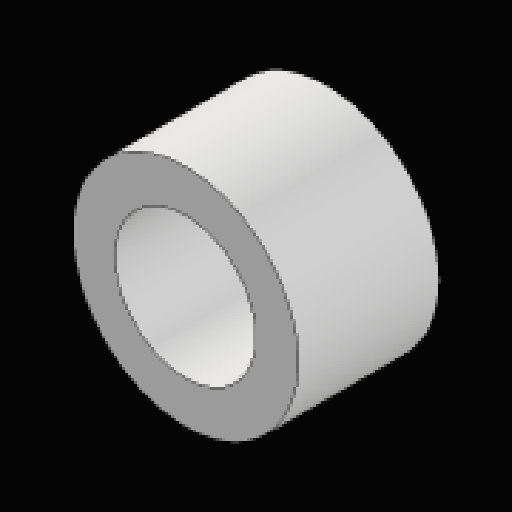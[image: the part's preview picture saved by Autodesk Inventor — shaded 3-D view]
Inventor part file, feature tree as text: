
AUTODESK INVENTOR PART (.ipt)
format: ipt  version: 2023.2 (Build 272271030, 271C)  size: 101,376 bytes
history: native  units: mm
features: extrude x1, sketch x1
ambient origin geometry x8: Origin, YZ Plane, XZ Plane, XY Plane, X Axis, Y Axis, Z Axis, Center Point
bodies: Solid1 (feature_tree)
feature tree (2):
  extrude  "Extrusion1"  Depth=5.0mm
  sketch  "Sketch1"  dims[d0=8.0mm d1=5.0mm d2=5.0mm d3=0.0mm]
